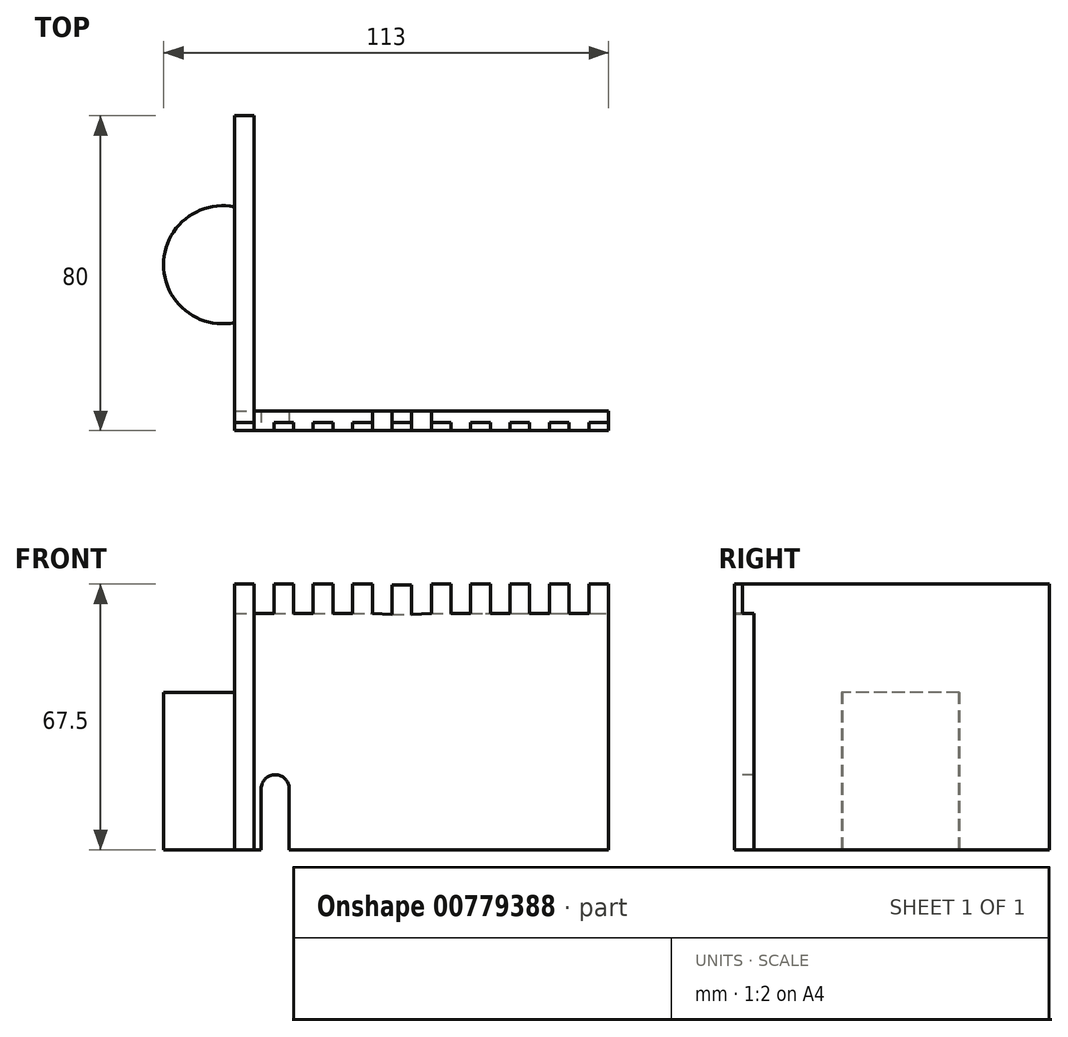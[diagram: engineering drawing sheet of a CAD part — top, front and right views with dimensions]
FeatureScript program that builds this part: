
annotation { "Feature Type Name" : "Feature", "Feature Type Description" : "" }
export const myFeature = defineFeature(function(context is Context, id is Id, definition is map)
    precondition{}
    {
        {
            var Q0;
            Q0=qCreatedBy(makeId("Front.planeOp"),FACE);
            var sketch = newSketch(context, id + "F0", { "sketchPlane" : qUnion([Q0])});
            skLineSegment(sketch, "E0", {"start": v(0, 0) * mm, "end": v(95, 0) * mm});
            skLineSegment(sketch, "E1", {"start": v(0, 0) * mm, "end": v(0, 60) * mm});
            skLineSegment(sketch, "E2.bottom", {"start": v(0, 60) * mm, "end": v(5, 60) * mm});
            skLineSegment(sketch, "E2.top", {"start": v(0, 67.5) * mm, "end": v(5, 67.5) * mm});
            skLineSegment(sketch, "E2.left", {"start": v(0, 60) * mm, "end": v(0, 67.5) * mm});
            skLineSegment(sketch, "E2.right", {"start": v(5, 60) * mm, "end": v(5, 67.5) * mm});
            skLineSegment(sketch, "E3.bottom", {"start": v(10, 60) * mm, "end": v(15, 60) * mm});
            skLineSegment(sketch, "E3.top", {"start": v(10, 67.5) * mm, "end": v(15, 67.5) * mm});
            skLineSegment(sketch, "E3.left", {"start": v(10, 60) * mm, "end": v(10, 67.5) * mm});
            skLineSegment(sketch, "E3.right", {"start": v(15, 60) * mm, "end": v(15, 67.5) * mm});
            skLineSegment(sketch, "E4.bottom", {"start": v(20, 60) * mm, "end": v(25, 60) * mm});
            skLineSegment(sketch, "E4.top", {"start": v(20, 67.5) * mm, "end": v(25, 67.5) * mm});
            skLineSegment(sketch, "E4.left", {"start": v(20, 60) * mm, "end": v(20, 67.5) * mm});
            skLineSegment(sketch, "E4.right", {"start": v(25, 60) * mm, "end": v(25, 67.5) * mm});
            skLineSegment(sketch, "E5.bottom", {"start": v(30, 60) * mm, "end": v(35, 60) * mm});
            skLineSegment(sketch, "E5.top", {"start": v(30, 67.5) * mm, "end": v(35, 67.5) * mm});
            skLineSegment(sketch, "E5.left", {"start": v(30, 60) * mm, "end": v(30, 67.5) * mm});
            skLineSegment(sketch, "E5.right", {"start": v(35, 60) * mm, "end": v(35, 67.5) * mm});
            skLineSegment(sketch, "E6.bottom", {"start": v(40, 59.82) * mm, "end": v(45, 59.82) * mm});
            skLineSegment(sketch, "E6.top", {"start": v(40, 67.32) * mm, "end": v(45, 67.32) * mm});
            skLineSegment(sketch, "E6.left", {"start": v(40, 59.82) * mm, "end": v(40, 67.32) * mm});
            skLineSegment(sketch, "E6.right", {"start": v(45, 59.82) * mm, "end": v(45, 67.32) * mm});
            skLineSegment(sketch, "E7.bottom", {"start": v(50, 60) * mm, "end": v(55, 60) * mm});
            skLineSegment(sketch, "E7.top", {"start": v(50, 67.5) * mm, "end": v(55, 67.5) * mm});
            skLineSegment(sketch, "E7.left", {"start": v(50, 60) * mm, "end": v(50, 67.5) * mm});
            skLineSegment(sketch, "E7.right", {"start": v(55, 60) * mm, "end": v(55, 67.5) * mm});
            skLineSegment(sketch, "E8.bottom", {"start": v(60, 60) * mm, "end": v(65, 60) * mm});
            skLineSegment(sketch, "E8.top", {"start": v(60, 67.5) * mm, "end": v(65, 67.5) * mm});
            skLineSegment(sketch, "E8.left", {"start": v(60, 60) * mm, "end": v(60, 67.5) * mm});
            skLineSegment(sketch, "E8.right", {"start": v(65, 60) * mm, "end": v(65, 67.5) * mm});
            skLineSegment(sketch, "E9.bottom", {"start": v(70, 60) * mm, "end": v(75, 60) * mm});
            skLineSegment(sketch, "E9.top", {"start": v(70, 67.5) * mm, "end": v(75, 67.5) * mm});
            skLineSegment(sketch, "E9.left", {"start": v(70, 60) * mm, "end": v(70, 67.5) * mm});
            skLineSegment(sketch, "E9.right", {"start": v(75, 60) * mm, "end": v(75, 67.5) * mm});
            skLineSegment(sketch, "E10.bottom", {"start": v(80, 60) * mm, "end": v(85, 60) * mm});
            skLineSegment(sketch, "E10.top", {"start": v(80, 67.5) * mm, "end": v(85, 67.5) * mm});
            skLineSegment(sketch, "E10.left", {"start": v(80, 60) * mm, "end": v(80, 67.5) * mm});
            skLineSegment(sketch, "E10.right", {"start": v(85, 60) * mm, "end": v(85, 67.5) * mm});
            skLineSegment(sketch, "E11.bottom", {"start": v(90, 60) * mm, "end": v(95, 60) * mm});
            skLineSegment(sketch, "E11.top", {"start": v(90, 67.5) * mm, "end": v(95, 67.5) * mm});
            skLineSegment(sketch, "E11.left", {"start": v(90, 60) * mm, "end": v(90, 67.5) * mm});
            skLineSegment(sketch, "E11.right", {"start": v(95, 60) * mm, "end": v(95, 67.5) * mm});
            skLineSegment(sketch, "E12", {"start": v(95, 60) * mm, "end": v(95, 0) * mm});
            skLineSegment(sketch, "E13", {"start": v(5, 60) * mm, "end": v(10, 60) * mm});
            skLineSegment(sketch, "E14", {"start": v(15, 60) * mm, "end": v(20, 60) * mm});
            skLineSegment(sketch, "E15", {"start": v(25, 60) * mm, "end": v(30, 60) * mm});
            skLineSegment(sketch, "E16", {"start": v(35, 60) * mm, "end": v(40, 59.82) * mm});
            skLineSegment(sketch, "E17", {"start": v(45, 59.82) * mm, "end": v(50, 60) * mm});
            skLineSegment(sketch, "E18", {"start": v(55, 60) * mm, "end": v(60, 60) * mm});
            skLineSegment(sketch, "E19", {"start": v(65, 60) * mm, "end": v(70, 60) * mm});
            skLineSegment(sketch, "E20", {"start": v(75, 60) * mm, "end": v(80, 60) * mm});
            skLineSegment(sketch, "E21", {"start": v(85, 60) * mm, "end": v(90, 60) * mm});
            skLineSegment(sketch, "E22", {"start": v(13.88, 0) * mm, "end": v(13.88, 15.53) * mm});
            skLineSegment(sketch, "E23", {"start": v(6.78, 15.53) * mm, "end": v(6.78, 0) * mm});
            skPoint(sketch, "E24.third.point", {"position": v(11.25, 18.96) * mm});
            skArc(sketch, "E25", {"start": v(13.88, 15.53) * mm, "mid": v(10.33, 19.08) * mm, "end": v(6.78, 15.53) * mm});
            skSolve(sketch);
        }
        {
            var Q0;
            Q0=qCreatedBy(makeId("Right.planeOp"),FACE);
            var sketch = newSketch(context, id + "F1", { "sketchPlane" : qUnion([Q0])});
            skLineSegment(sketch, "E26.bottom", {"start": v(0, 0) * mm, "end": v(80, 0) * mm});
            skLineSegment(sketch, "E26.top", {"start": v(0, 67.5) * mm, "end": v(80, 67.5) * mm});
            skLineSegment(sketch, "E26.left", {"start": v(0, 0) * mm, "end": v(0, 67.5) * mm});
            skLineSegment(sketch, "E26.right", {"start": v(80, 0) * mm, "end": v(80, 67.5) * mm});
            skSolve(sketch);
        }
        {
            var Q0;
            Q0=qCreatedBy(makeId("Top.planeOp"),FACE);
            var sketch = newSketch(context, id + "F2", { "sketchPlane" : qUnion([Q0])});
            skCircle(sketch, "E27", {"center": v(-3, 42.15) * mm, "radius": 15 * mm});
            skLineSegment(sketch, "E28", {"start": v(0, 56.84) * mm, "end": v(0, 27.45) * mm});
            skSolve(sketch);
        }
        {
            var Q0;
            {var subQ0=sQuery(id+"F2.wireOp",EDGE,"E28");Q0=makeQuery(id+"F2.imprint","IMPRINT",FACE,{"disambiguationData":[TD([[makeQuery(id+"F2.imprint","IMPRINT",EDGE,{"derivedFrom":subQ0}),-1.0]])]});}
            extrude(context, id + "F3", {"entities" : qUnion([Q0]), "depth" : 40 * mm, "offsetDistance" : 25 * mm});
        }
        {
            var Q0;
            {var subQ1=sQuery(id+"F0.wireOp",EDGE,"E1");Q0=makeQuery(id+"F0.imprint","IMPRINT",FACE,{"disambiguationData":[TD([[makeQuery(id+"F0.imprint","IMPRINT",EDGE,{"derivedFrom":subQ1}),-1.0]])]});}
            extrude(context, id + "F4", {"entities" : qUnion([Q0]), "depth" : -5 * mm, "offsetDistance" : 25 * mm});
        }
        {
            var Q0;
            Q0=makeQuery(id+"F0.imprint","IMPRINT",FACE,{"disambiguationData":[TD([[makeQuery(id+"F0.imprint","IMPRINT",EDGE,{"derivedFrom":sQuery(id+"F0.wireOp",EDGE,"E2.bottom")}),1.0]])]});
            var Q1;
            Q1=makeQuery(id+"F0.imprint","IMPRINT",FACE,{"disambiguationData":[TD([[makeQuery(id+"F0.imprint","IMPRINT",EDGE,{"derivedFrom":sQuery(id+"F0.wireOp",EDGE,"E3.bottom")}),1.0]])]});
            var Q2;
            Q2=makeQuery(id+"F0.imprint","IMPRINT",FACE,{"disambiguationData":[TD([[makeQuery(id+"F0.imprint","IMPRINT",EDGE,{"derivedFrom":sQuery(id+"F0.wireOp",EDGE,"E4.bottom")}),1.0]])]});
            var Q3;
            Q3=makeQuery(id+"F0.imprint","IMPRINT",FACE,{"disambiguationData":[TD([[makeQuery(id+"F0.imprint","IMPRINT",EDGE,{"derivedFrom":sQuery(id+"F0.wireOp",EDGE,"E5.bottom")}),1.0]])]});
            var Q4;
            Q4=makeQuery(id+"F0.imprint","IMPRINT",FACE,{"disambiguationData":[TD([[makeQuery(id+"F0.imprint","IMPRINT",EDGE,{"derivedFrom":sQuery(id+"F0.wireOp",EDGE,"E6.bottom")}),1.0]])]});
            var Q5;
            Q5=makeQuery(id+"F0.imprint","IMPRINT",FACE,{"disambiguationData":[TD([[makeQuery(id+"F0.imprint","IMPRINT",EDGE,{"derivedFrom":sQuery(id+"F0.wireOp",EDGE,"E7.bottom")}),1.0]])]});
            var Q6;
            Q6=makeQuery(id+"F0.imprint","IMPRINT",FACE,{"disambiguationData":[TD([[makeQuery(id+"F0.imprint","IMPRINT",EDGE,{"derivedFrom":sQuery(id+"F0.wireOp",EDGE,"E8.bottom")}),1.0]])]});
            var Q7;
            Q7=makeQuery(id+"F0.imprint","IMPRINT",FACE,{"disambiguationData":[TD([[makeQuery(id+"F0.imprint","IMPRINT",EDGE,{"derivedFrom":sQuery(id+"F0.wireOp",EDGE,"E9.bottom")}),1.0]])]});
            var Q8;
            Q8=makeQuery(id+"F0.imprint","IMPRINT",FACE,{"disambiguationData":[TD([[makeQuery(id+"F0.imprint","IMPRINT",EDGE,{"derivedFrom":sQuery(id+"F0.wireOp",EDGE,"E10.bottom")}),1.0]])]});
            var Q9;
            Q9=makeQuery(id+"F0.imprint","IMPRINT",FACE,{"disambiguationData":[TD([[makeQuery(id+"F0.imprint","IMPRINT",EDGE,{"derivedFrom":sQuery(id+"F0.wireOp",EDGE,"E11.bottom")}),1.0]])]});
            extrude(context, id + "F5", {"entities" : qUnion([Q0, Q1, Q2, Q3, Q4, Q5, Q6, Q7, Q8, Q9]), "operationType" : NewBodyOperationType.ADD, "depth" : -2 * mm, "offsetDistance" : 25 * mm});
        }
        {
            var Q0;
            Q0=makeQuery(id+"F1.imprint","IMPRINT",FACE,{"disambiguationData":[TD([[makeQuery(id+"F1.imprint","IMPRINT",EDGE,{"derivedFrom":sQuery(id+"F1.wireOp",EDGE,"E26.bottom")}),1.0]])]});
            extrude(context, id + "F6", {"entities" : qUnion([Q0]), "depth" : 5 * mm, "offsetDistance" : 25 * mm});
        }
    });
